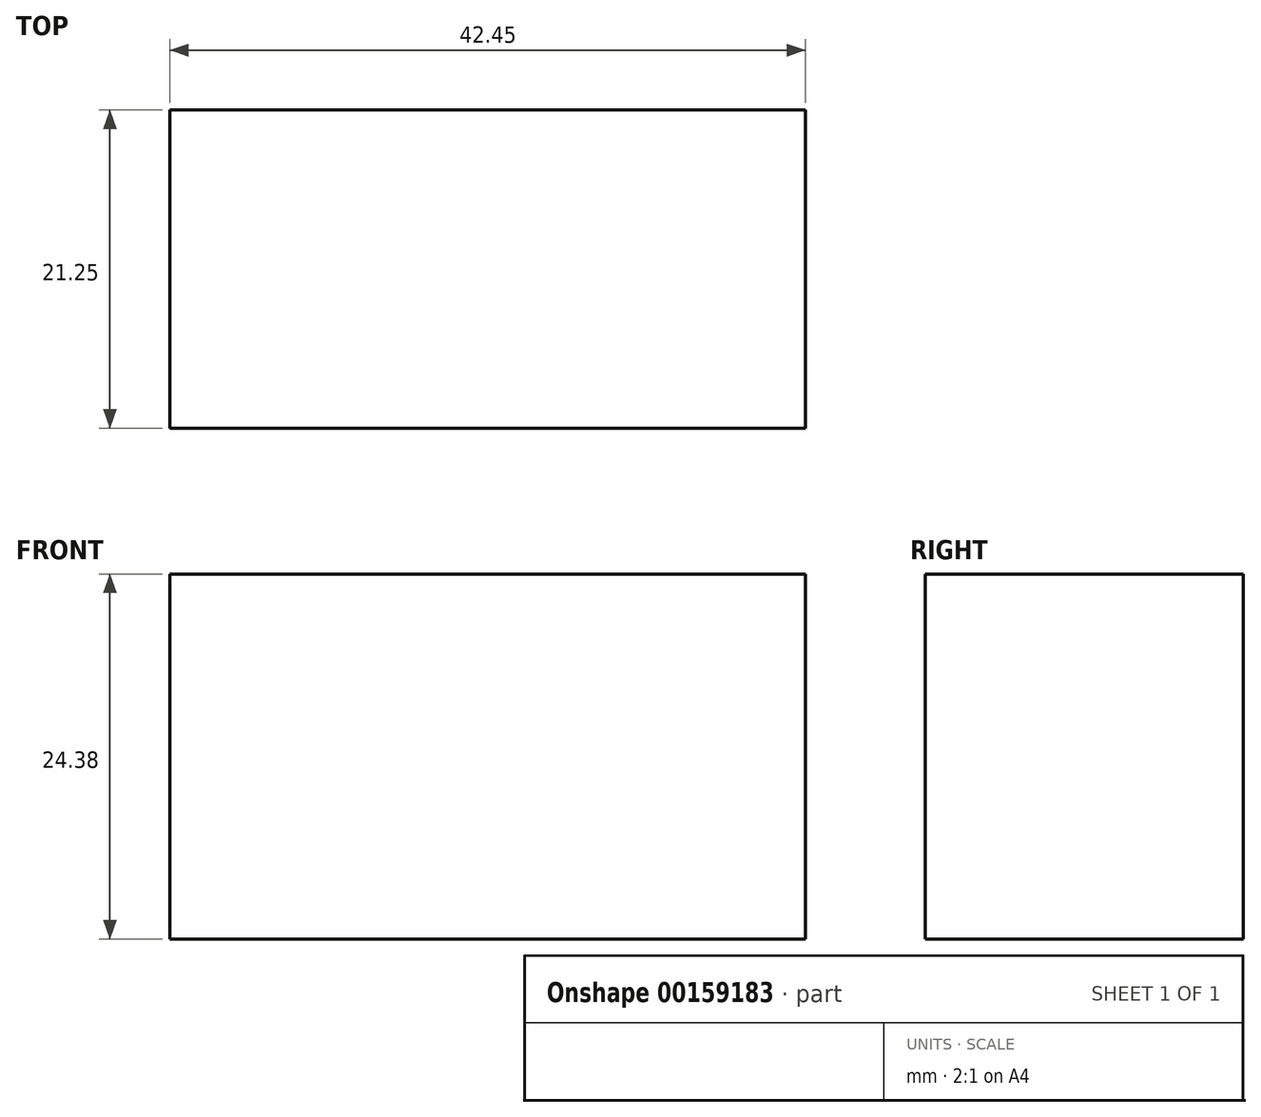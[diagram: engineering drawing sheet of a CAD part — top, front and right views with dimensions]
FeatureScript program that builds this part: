
annotation { "Feature Type Name" : "Feature", "Feature Type Description" : "" }
export const myFeature = defineFeature(function(context is Context, id is Id, definition is map)
    precondition{}
    {
        {
            var Q0;
            Q0=qCreatedBy(makeId("Top.planeOp"),FACE);
            var sketch = newSketch(context, id + "F0", { "sketchPlane" : qUnion([Q0])});
            skCircle(sketch, "E0", {"center": v(-39.97, -29.01) * mm, "radius": 32.93 * mm});
            skCircle(sketch, "E1", {"center": v(-39.97, -29.01) * mm, "radius": 25.82 * mm});
            skCircle(sketch, "E2", {"center": v(-39.97, -29.01) * mm, "radius": 49.39 * mm});
            skCircle(sketch, "E3", {"center": v(-44.78, -3.64) * mm, "radius": 17.48 * mm});
            skLineSegment(sketch, "E4.bottom", {"start": v(-26.08, 67.17) * mm, "end": v(31.1, 67.17) * mm});
            skLineSegment(sketch, "E4.top", {"start": v(-19.73, 25) * mm, "end": v(37.44, 25) * mm});
            skLineSegment(sketch, "E4.left", {"start": v(-26.08, 67.17) * mm, "end": v(-26.08, 31.34) * mm});
            skLineSegment(sketch, "E4.right", {"start": v(37.44, 60.82) * mm, "end": v(37.44, 25) * mm});
            skLineSegment(sketch, "E5.bottom", {"start": v(-26.08, 45.92) * mm, "end": v(16.37, 45.92) * mm});
            skLineSegment(sketch, "E5.top", {"start": v(-26.08, 67.17) * mm, "end": v(16.37, 67.17) * mm});
            skLineSegment(sketch, "E5.left", {"start": v(-26.08, 45.92) * mm, "end": v(-26.08, 67.17) * mm});
            skLineSegment(sketch, "E5.right", {"start": v(16.37, 45.92) * mm, "end": v(16.37, 67.17) * mm});
            skPoint(sketch, "E6.visualSharp", {"position": v(-26.08, 25) * mm});
            skArc(sketch, "E6.filletArc", {"start": v(-26.08, 31.34) * mm, "mid": v(-24.22, 26.85) * mm, "end": v(-19.73, 25) * mm});
            skPoint(sketch, "E7.visualSharp", {"position": v(37.44, 67.17) * mm});
            skArc(sketch, "E7.filletArc", {"start": v(37.44, 60.82) * mm, "mid": v(35.58, 65.3) * mm, "end": v(31.1, 67.17) * mm});
            skCircle(sketch, "E8", {"center": v(42.61, -10.95) * mm, "radius": 34.19 * mm});
            skPoint(sketch, "E8.first.point", {"position": v(21.24, 15.73) * mm});
            skPoint(sketch, "E8.second.point", {"position": v(33.58, -43.93) * mm});
            skPoint(sketch, "E8.third.point", {"position": v(13.27, -28.5) * mm});
            skSolve(sketch);
        }
        {
            var Q0;
            Q0=makeQuery(id+"F0.imprint","IMPRINT",FACE,{"disambiguationData":[TD([[makeQuery(id+"F0.imprint","IMPRINT",EDGE,{"derivedFrom":sQuery(id+"F0.wireOp",EDGE,"E5.bottom")}),1.0]])]});
            extrude(context, id + "F1", {"entities" : qUnion([Q0]), "depth" : 24.38 * mm, "offsetDistance" : 25.4 * mm});
        }
    });
